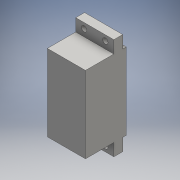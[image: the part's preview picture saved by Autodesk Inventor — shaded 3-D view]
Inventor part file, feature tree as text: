
AUTODESK INVENTOR PART (.ipt)
format: ipt  version: 2016 (Build 200138000, 138)  size: 133,632 bytes
history: native  units: mm
features: extrude x5, sketch x5, other x1
ambient origin geometry x8: Origin, YZ Plane, XZ Plane, XY Plane, X Axis, Y Axis, Z Axis, Center Point
bodies: Body1 (feature_tree)
feature tree (11):
  other  "ソリッド1"
  extrude  "押し出し1"  Depth=21.5mm
  extrude  "押し出し2"  Depth=43.2mm
  extrude  "押し出し3"  Depth=16.0mm TaperAngle=0.0deg
  extrude  "押し出し4"  Depth=57.2mm
  extrude  "押し出し5"  Depth=5.0mm TaperAngle=0.0deg
  sketch  "スケッチ1"
  sketch  "スケッチ2"
  sketch  "スケッチ3"
  sketch  "スケッチ4"
  sketch  "スケッチ5"
